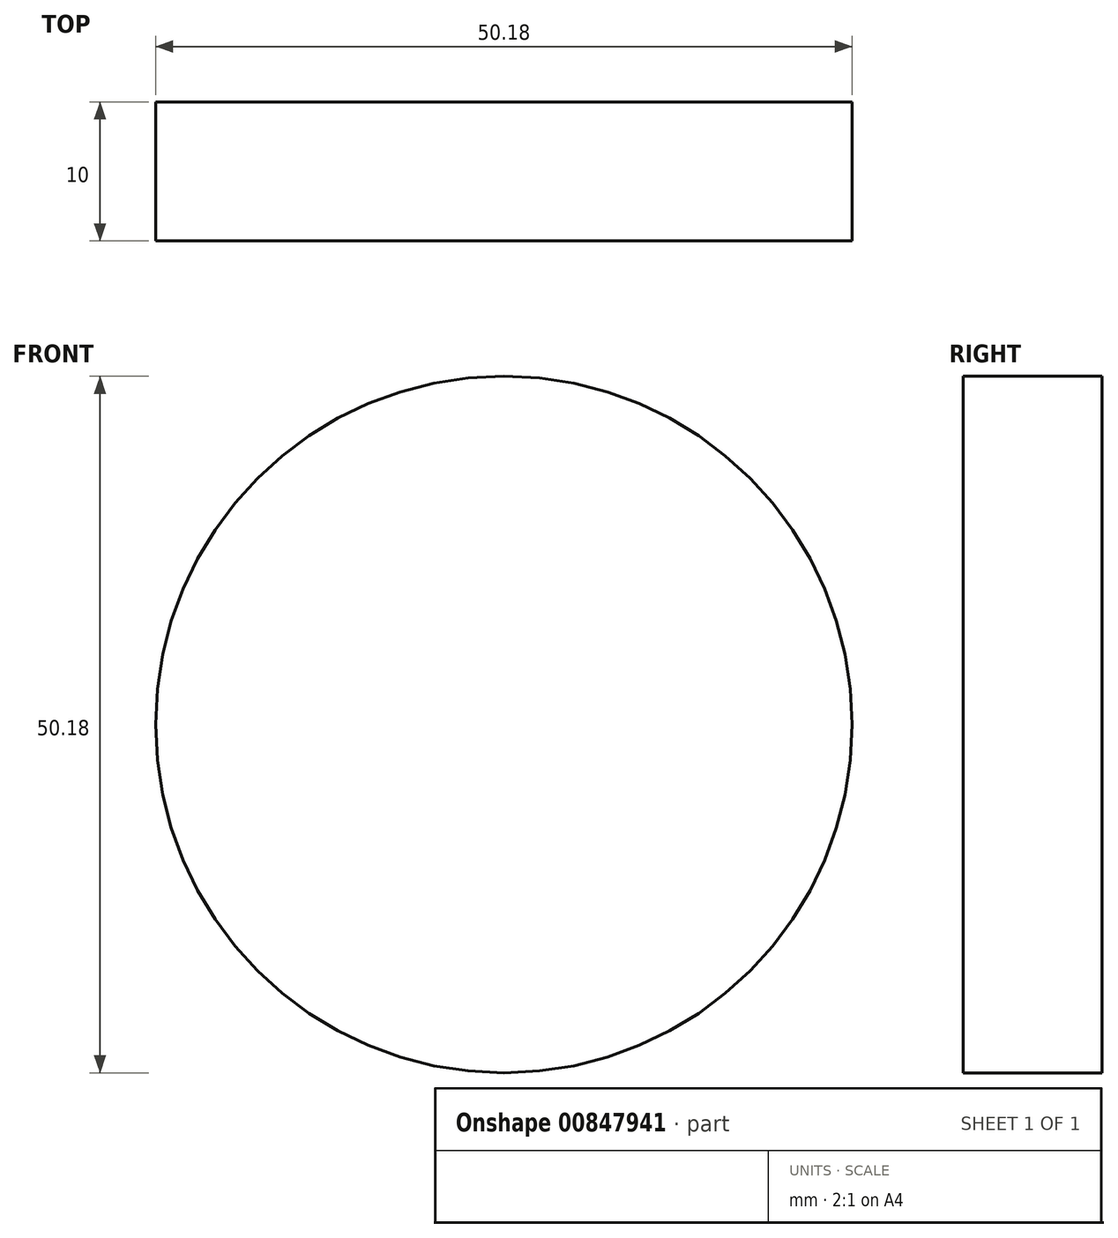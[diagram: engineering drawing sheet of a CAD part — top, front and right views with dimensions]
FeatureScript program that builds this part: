
annotation { "Feature Type Name" : "Feature", "Feature Type Description" : "" }
export const myFeature = defineFeature(function(context is Context, id is Id, definition is map)
    precondition{}
    {
        {
            var Q0;
            Q0=qCreatedBy(makeId("Front.planeOp"),FACE);
            var sketch = newSketch(context, id + "F0", { "sketchPlane" : qUnion([Q0])});
            skCircle(sketch, "E0", {"center": v(0, 0) * mm, "radius": 25.09 * mm});
            skSolve(sketch);
        }
        {
            var Q0;
            Q0=makeQuery(id+"F0.imprint","IMPRINT",FACE,{"disambiguationData":[TD([[makeQuery(id+"F0.imprint","IMPRINT",EDGE,{"derivedFrom":sQuery(id+"F0.wireOp",EDGE,"E0")}),1.0]])]});
            extrude(context, id + "F1", {"entities" : qUnion([Q0]), "depth" : 10 * mm, "offsetDistance" : 25 * mm});
        }
    });
